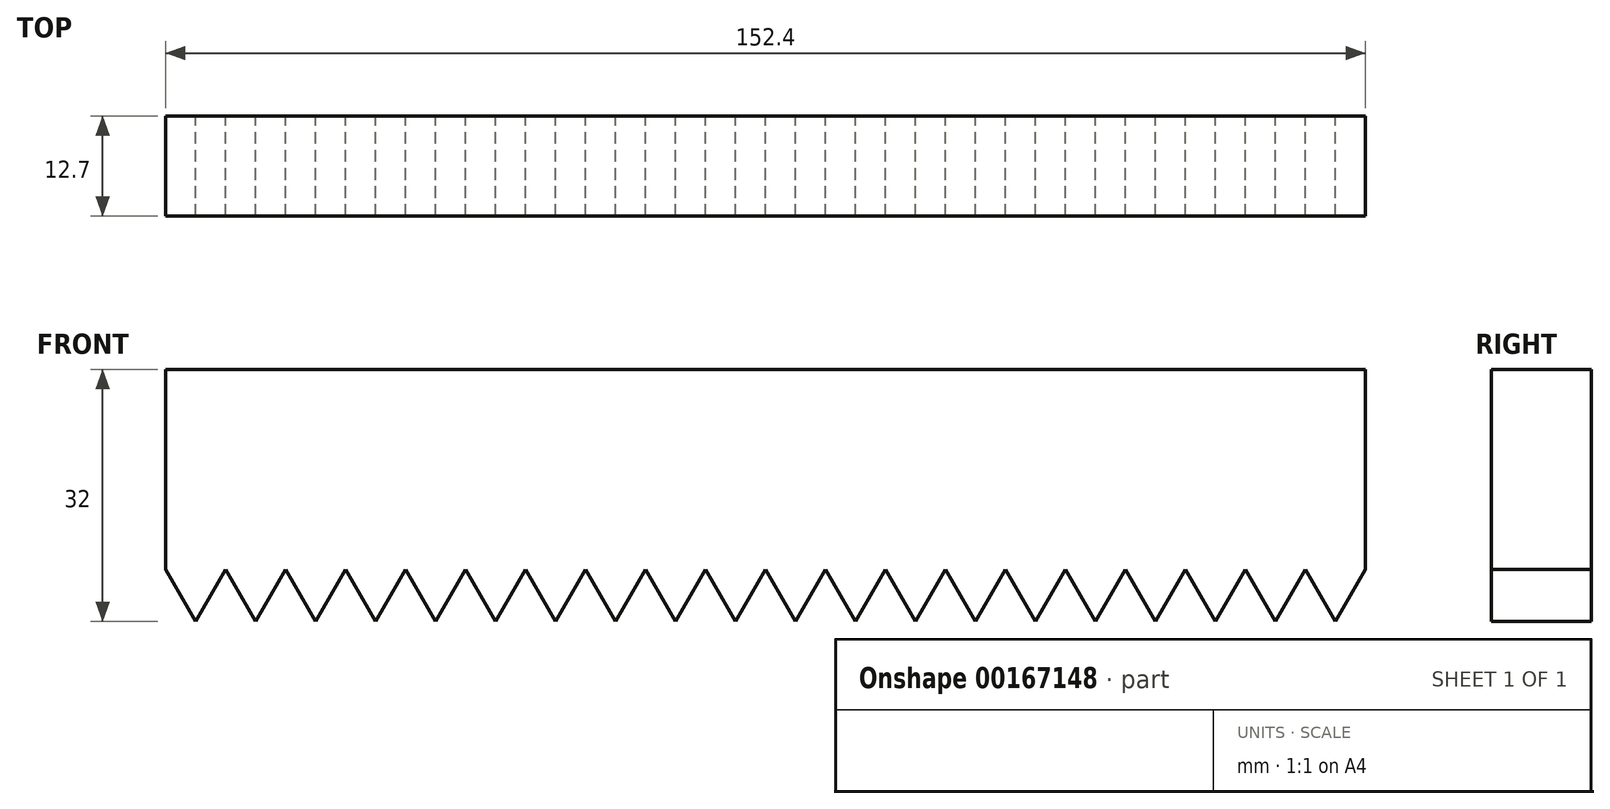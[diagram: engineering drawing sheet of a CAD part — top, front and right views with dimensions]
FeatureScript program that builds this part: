
annotation { "Feature Type Name" : "Feature", "Feature Type Description" : "" }
export const myFeature = defineFeature(function(context is Context, id is Id, definition is map)
    precondition{}
    {
        {
            var Q0;
            Q0=qCreatedBy(makeId("Front.planeOp"),FACE);
            var sketch = newSketch(context, id + "F0", { "sketchPlane" : qUnion([Q0])});
            skLineSegment(sketch, "E0.bottom", {"start": v(76.2, 12.7) * mm, "end": v(-76.2, 12.7) * mm});
            skLineSegment(sketch, "E0.top", {"start": v(76.2, -12.7) * mm, "end": v(-76.2, -12.7) * mm});
            skLineSegment(sketch, "E0.left", {"start": v(76.2, 12.7) * mm, "end": v(76.2, -12.7) * mm});
            skLineSegment(sketch, "E0.right", {"start": v(-76.2, 12.7) * mm, "end": v(-76.2, -12.7) * mm});
            skPoint(sketch, "E0.middle", {"position": v(0, 0) * mm});
            skLineSegment(sketch, "E1", {"start": v(-76.2, -12.7) * mm, "end": v(-72.39, -19.3) * mm});
            skLineSegment(sketch, "E2", {"start": v(-72.39, -19.3) * mm, "end": v(-68.58, -12.7) * mm});
            skLineSegment(sketch, "E3.1.0.0", {"start": v(83.82, -12.7) * mm, "end": v(-68.58, -12.7) * mm});
            skLineSegment(sketch, "E3.1.0.1", {"start": v(-68.58, -12.7) * mm, "end": v(-64.77, -19.3) * mm});
            skLineSegment(sketch, "E3.1.0.2", {"start": v(-64.77, -19.3) * mm, "end": v(-60.96, -12.7) * mm});
            skLineSegment(sketch, "E3.2.0.0", {"start": v(91.44, -12.7) * mm, "end": v(-60.96, -12.7) * mm});
            skLineSegment(sketch, "E3.2.0.1", {"start": v(-60.96, -12.7) * mm, "end": v(-57.15, -19.3) * mm});
            skLineSegment(sketch, "E3.2.0.2", {"start": v(-57.15, -19.3) * mm, "end": v(-53.34, -12.7) * mm});
            skLineSegment(sketch, "E3.3.0.0", {"start": v(99.06, -12.7) * mm, "end": v(-53.34, -12.7) * mm});
            skLineSegment(sketch, "E3.3.0.1", {"start": v(-53.34, -12.7) * mm, "end": v(-49.53, -19.3) * mm});
            skLineSegment(sketch, "E3.3.0.2", {"start": v(-49.53, -19.3) * mm, "end": v(-45.72, -12.7) * mm});
            skLineSegment(sketch, "E3.4.0.0", {"start": v(106.68, -12.7) * mm, "end": v(-45.72, -12.7) * mm});
            skLineSegment(sketch, "E3.4.0.1", {"start": v(-45.72, -12.7) * mm, "end": v(-41.9, -19.3) * mm});
            skLineSegment(sketch, "E3.4.0.2", {"start": v(-41.9, -19.3) * mm, "end": v(-38.1, -12.7) * mm});
            skLineSegment(sketch, "E3.5.0.0", {"start": v(114.3, -12.7) * mm, "end": v(-38.1, -12.7) * mm});
            skLineSegment(sketch, "E3.5.0.1", {"start": v(-38.1, -12.7) * mm, "end": v(-34.29, -19.3) * mm});
            skLineSegment(sketch, "E3.5.0.2", {"start": v(-34.29, -19.3) * mm, "end": v(-30.48, -12.7) * mm});
            skLineSegment(sketch, "E3.6.0.0", {"start": v(121.92, -12.7) * mm, "end": v(-30.48, -12.7) * mm});
            skLineSegment(sketch, "E3.6.0.1", {"start": v(-30.48, -12.7) * mm, "end": v(-26.67, -19.3) * mm});
            skLineSegment(sketch, "E3.6.0.2", {"start": v(-26.67, -19.3) * mm, "end": v(-22.86, -12.7) * mm});
            skLineSegment(sketch, "E3.7.0.0", {"start": v(129.54, -12.7) * mm, "end": v(-22.86, -12.7) * mm});
            skLineSegment(sketch, "E3.7.0.1", {"start": v(-22.86, -12.7) * mm, "end": v(-19.05, -19.3) * mm});
            skLineSegment(sketch, "E3.7.0.2", {"start": v(-19.05, -19.3) * mm, "end": v(-15.24, -12.7) * mm});
            skLineSegment(sketch, "E3.8.0.0", {"start": v(137.16, -12.7) * mm, "end": v(-15.24, -12.7) * mm});
            skLineSegment(sketch, "E3.8.0.1", {"start": v(-15.24, -12.7) * mm, "end": v(-11.43, -19.3) * mm});
            skLineSegment(sketch, "E3.8.0.2", {"start": v(-11.43, -19.3) * mm, "end": v(-7.62, -12.7) * mm});
            skLineSegment(sketch, "E3.9.0.0", {"start": v(144.78, -12.7) * mm, "end": v(-7.62, -12.7) * mm});
            skLineSegment(sketch, "E3.9.0.1", {"start": v(-7.62, -12.7) * mm, "end": v(-3.8, -19.3) * mm});
            skLineSegment(sketch, "E3.9.0.2", {"start": v(-3.8, -19.3) * mm, "end": v(0, -12.7) * mm});
            skLineSegment(sketch, "E3.10.0.0", {"start": v(152.4, -12.7) * mm, "end": v(0, -12.7) * mm});
            skLineSegment(sketch, "E3.10.0.1", {"start": v(0, -12.7) * mm, "end": v(3.81, -19.3) * mm});
            skLineSegment(sketch, "E3.10.0.2", {"start": v(3.81, -19.3) * mm, "end": v(7.62, -12.7) * mm});
            skLineSegment(sketch, "E3.11.0.0", {"start": v(160.02, -12.7) * mm, "end": v(7.62, -12.7) * mm});
            skLineSegment(sketch, "E3.11.0.1", {"start": v(7.62, -12.7) * mm, "end": v(11.43, -19.3) * mm});
            skLineSegment(sketch, "E3.11.0.2", {"start": v(11.43, -19.3) * mm, "end": v(15.24, -12.7) * mm});
            skLineSegment(sketch, "E3.12.0.0", {"start": v(167.64, -12.7) * mm, "end": v(15.24, -12.7) * mm});
            skLineSegment(sketch, "E3.12.0.1", {"start": v(15.24, -12.7) * mm, "end": v(19.05, -19.3) * mm});
            skLineSegment(sketch, "E3.12.0.2", {"start": v(19.05, -19.3) * mm, "end": v(22.86, -12.7) * mm});
            skLineSegment(sketch, "E3.13.0.0", {"start": v(175.26, -12.7) * mm, "end": v(22.86, -12.7) * mm});
            skLineSegment(sketch, "E3.13.0.1", {"start": v(22.86, -12.7) * mm, "end": v(26.67, -19.3) * mm});
            skLineSegment(sketch, "E3.13.0.2", {"start": v(26.67, -19.3) * mm, "end": v(30.48, -12.7) * mm});
            skLineSegment(sketch, "E3.14.0.0", {"start": v(182.88, -12.7) * mm, "end": v(30.48, -12.7) * mm});
            skLineSegment(sketch, "E3.14.0.1", {"start": v(30.48, -12.7) * mm, "end": v(34.3, -19.3) * mm});
            skLineSegment(sketch, "E3.14.0.2", {"start": v(34.3, -19.3) * mm, "end": v(38.1, -12.7) * mm});
            skLineSegment(sketch, "E3.15.0.0", {"start": v(190.5, -12.7) * mm, "end": v(38.1, -12.7) * mm});
            skLineSegment(sketch, "E3.15.0.1", {"start": v(38.1, -12.7) * mm, "end": v(41.91, -19.3) * mm});
            skLineSegment(sketch, "E3.15.0.2", {"start": v(41.91, -19.3) * mm, "end": v(45.72, -12.7) * mm});
            skLineSegment(sketch, "E3.16.0.0", {"start": v(198.12, -12.7) * mm, "end": v(45.72, -12.7) * mm});
            skLineSegment(sketch, "E3.16.0.1", {"start": v(45.72, -12.7) * mm, "end": v(49.53, -19.3) * mm});
            skLineSegment(sketch, "E3.16.0.2", {"start": v(49.53, -19.3) * mm, "end": v(53.34, -12.7) * mm});
            skLineSegment(sketch, "E3.17.0.0", {"start": v(205.74, -12.7) * mm, "end": v(53.34, -12.7) * mm});
            skLineSegment(sketch, "E3.17.0.1", {"start": v(53.34, -12.7) * mm, "end": v(57.15, -19.3) * mm});
            skLineSegment(sketch, "E3.17.0.2", {"start": v(57.15, -19.3) * mm, "end": v(60.96, -12.7) * mm});
            skLineSegment(sketch, "E3.18.0.0", {"start": v(213.36, -12.7) * mm, "end": v(60.96, -12.7) * mm});
            skLineSegment(sketch, "E3.18.0.1", {"start": v(60.96, -12.7) * mm, "end": v(64.77, -19.3) * mm});
            skLineSegment(sketch, "E3.18.0.2", {"start": v(64.77, -19.3) * mm, "end": v(68.58, -12.7) * mm});
            skLineSegment(sketch, "E3.19.0.0", {"start": v(220.98, -12.7) * mm, "end": v(68.58, -12.7) * mm});
            skLineSegment(sketch, "E3.19.0.1", {"start": v(68.58, -12.7) * mm, "end": v(72.4, -19.3) * mm});
            skLineSegment(sketch, "E3.19.0.2", {"start": v(72.4, -19.3) * mm, "end": v(76.2, -12.7) * mm});
            skLineSegment(sketch, "E3.direction1", {"start": v(-72.39, -19.3) * mm, "end": v(-64.77, -19.3) * mm, "construction": true});
            skSolve(sketch);
        }
        {
            var Q0;
            Q0 = qSketchRegion(id + "F0", true);
            extrude(context, id + "F1", {"entities" : qUnion([Q0]), "depth" : 12.7 * mm});
        }
    });
